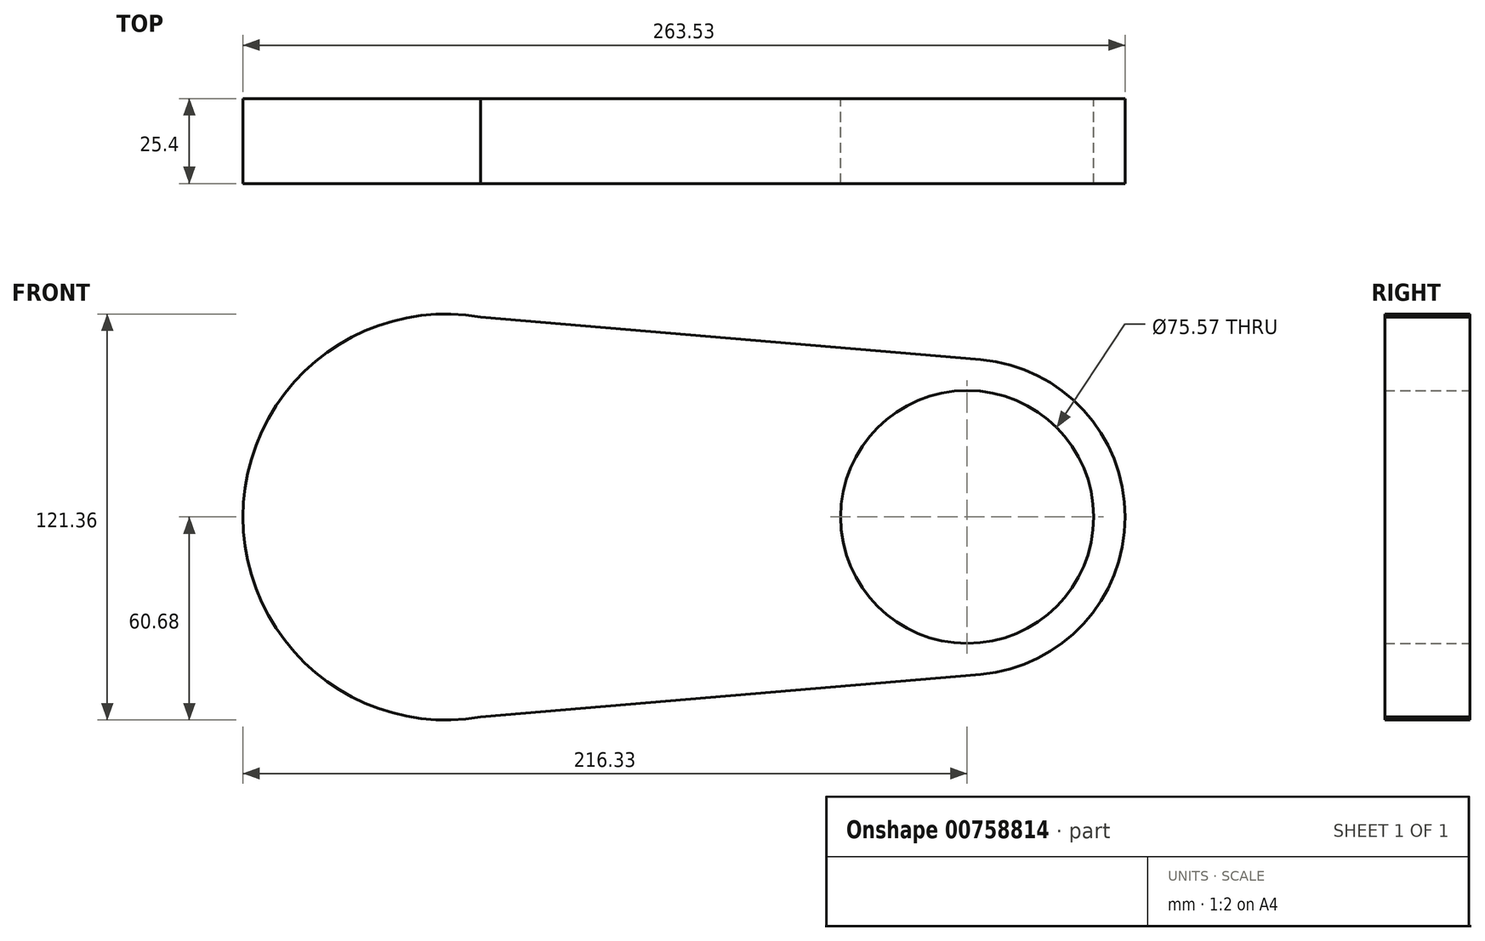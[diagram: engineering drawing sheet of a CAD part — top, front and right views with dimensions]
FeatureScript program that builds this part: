
annotation { "Feature Type Name" : "Feature", "Feature Type Description" : "" }
export const myFeature = defineFeature(function(context is Context, id is Id, definition is map)
    precondition{}
    {
        {
            var Q0;
            Q0=qCreatedBy(makeId("Front.planeOp"),FACE);
            var sketch = newSketch(context, id + "F0", { "sketchPlane" : qUnion([Q0])});
            skCircle(sketch, "E0", {"center": v(0, 0) * mm, "radius": 60.68 * mm});
            skCircle(sketch, "E1", {"center": v(155.65, 0) * mm, "radius": 37.78 * mm});
            skCircle(sketch, "E2", {"center": v(155.65, 0) * mm, "radius": 47.2 * mm});
            skLineSegment(sketch, "E3", {"start": v(0, 60.68) * mm, "end": v(159.67, 47.03) * mm});
            skLineSegment(sketch, "E4", {"start": v(0, -60.68) * mm, "end": v(159.67, -47.03) * mm});
            skCircle(sketch, "E5", {"center": v(0, 0) * mm, "radius": 50.8 * mm});
            skSolve(sketch);
        }
        {
            var Q0;
            Q0 = qSketchRegion(id + "F0", true);
            var Q1;
            {var subQ0=sQuery(id+"F0.wireOp",EDGE,"E3");var subQ1=sQuery(id+"F0.wireOp",EDGE,"E0");var subQ2=makeQuery(id+"F0.imprint","INTERSECT",VERTEX,{"disambiguationData":[OD(1.0)],"derivedFrom":[subQ1,subQ0]});Q1=makeQuery(id+"F0.imprint","IMPRINT",FACE,{"disambiguationData":[TD([[makeQuery(id+"F0.imprint","IMPRINT",EDGE,{"disambiguationData":[TD([[subQ2,1.0]])],"derivedFrom":subQ1}),-1.0]])]});}
            extrude(context, id + "F1", {"entities" : qUnion([Q0, Q1]), "depth" : 25.4 * mm, "offsetDistance" : 25.4 * mm});
        }
        {
            var Q0;
            Q0=qCreatedBy(makeId("Front.planeOp"),FACE);
            var sketch = newSketch(context, id + "F2", { "sketchPlane" : qUnion([Q0])});
            skCircle(sketch, "E6", {"center": v(0, 0) * mm, "radius": 61.97 * mm});
            skCircle(sketch, "E7", {"center": v(0, 0) * mm, "radius": 52.6 * mm});
            skSolve(sketch);
        }
        {
            var Q0;
            Q0=makeQuery(id+"F2.imprint","IMPRINT",FACE,{"disambiguationData":[TD([[makeQuery(id+"F2.imprint","IMPRINT",EDGE,{"derivedFrom":sQuery(id+"F2.wireOp",EDGE,"E7")}),1.0]])]});
            extrude(context, id + "F3", {"entities" : qUnion([Q0]), "operationType" : NewBodyOperationType.ADD, "depth" : 25.4 * mm, "offsetDistance" : 25.4 * mm});
        }
    });
